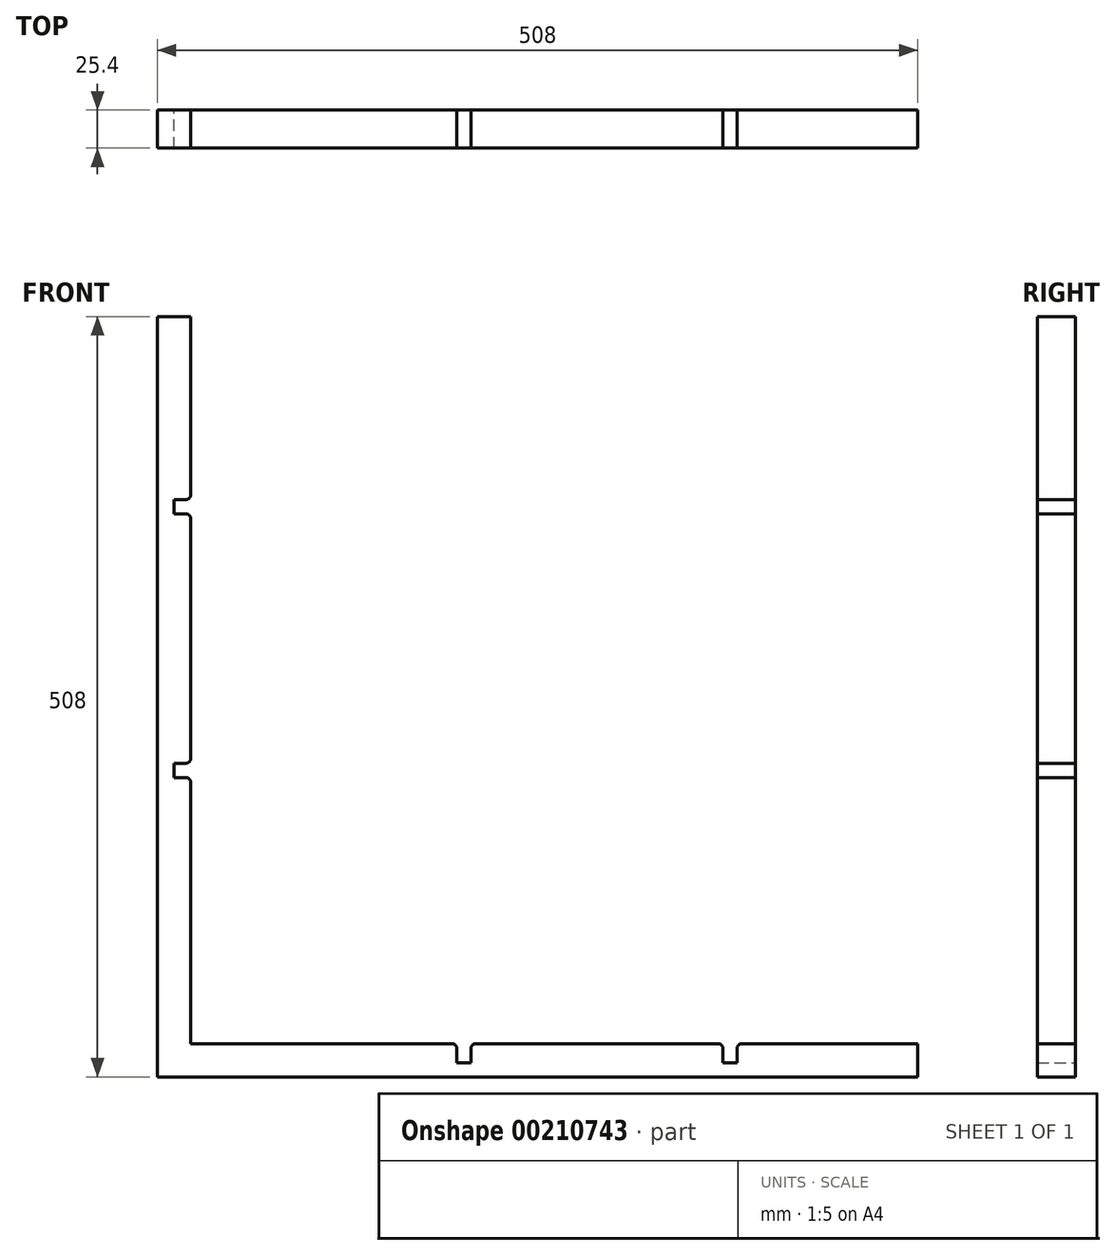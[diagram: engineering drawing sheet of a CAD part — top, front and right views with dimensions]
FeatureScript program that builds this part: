
annotation { "Feature Type Name" : "Feature", "Feature Type Description" : "" }
export const myFeature = defineFeature(function(context is Context, id is Id, definition is map)
    precondition{}
    {
        {
            var Q0;
            Q0=qCreatedBy(makeId("Front.planeOp"),FACE);
            var sketch = newSketch(context, id + "F0", { "sketchPlane" : qUnion([Q0])});
            skLineSegment(sketch, "E0", {"start": v(-317.84, 287.42) * mm, "end": v(-317.84, -220.58) * mm});
            skLineSegment(sketch, "E1", {"start": v(-317.84, -220.58) * mm, "end": v(190.16, -220.58) * mm});
            skLineSegment(sketch, "E2", {"start": v(-295.62, 287.42) * mm, "end": v(-317.84, 287.42) * mm});
            skLineSegment(sketch, "E3", {"start": v(190.16, -220.58) * mm, "end": v(190.16, -198.36) * mm});
            skLineSegment(sketch, "E4", {"start": v(190.16, -198.36) * mm, "end": v(72.68, -198.36) * mm});
            skLineSegment(sketch, "E5", {"start": v(69.5, -201.53) * mm, "end": v(69.5, -211.06) * mm});
            skLineSegment(sketch, "E6", {"start": v(69.5, -211.06) * mm, "end": v(59.98, -211.06) * mm});
            skLineSegment(sketch, "E7", {"start": v(59.98, -211.06) * mm, "end": v(59.98, -201.53) * mm});
            skLineSegment(sketch, "E8", {"start": v(56.8, -198.36) * mm, "end": v(-105.12, -198.36) * mm});
            skLineSegment(sketch, "E9", {"start": v(-108.3, -201.53) * mm, "end": v(-108.3, -211.06) * mm});
            skLineSegment(sketch, "E10", {"start": v(-108.3, -211.06) * mm, "end": v(-117.82, -211.06) * mm});
            skLineSegment(sketch, "E11", {"start": v(-117.82, -211.06) * mm, "end": v(-117.82, -201.53) * mm});
            skLineSegment(sketch, "E12", {"start": v(-121, -198.36) * mm, "end": v(-295.62, -198.36) * mm});
            skLineSegment(sketch, "E13", {"start": v(-295.62, -198.36) * mm, "end": v(-295.62, -23.73) * mm});
            skLineSegment(sketch, "E14", {"start": v(-298.8, -20.56) * mm, "end": v(-306.67, -20.56) * mm});
            skLineSegment(sketch, "E15", {"start": v(-306.67, -20.56) * mm, "end": v(-306.67, -11.03) * mm});
            skLineSegment(sketch, "E16", {"start": v(-306.67, -11.03) * mm, "end": v(-298.8, -11.03) * mm});
            skLineSegment(sketch, "E17", {"start": v(-295.62, -7.86) * mm, "end": v(-295.62, 152.42) * mm});
            skLineSegment(sketch, "E18", {"start": v(-298.8, 155.6) * mm, "end": v(-306.67, 155.6) * mm});
            skLineSegment(sketch, "E19", {"start": v(-306.67, 155.6) * mm, "end": v(-306.67, 165.12) * mm});
            skLineSegment(sketch, "E20", {"start": v(-306.67, 165.12) * mm, "end": v(-298.8, 165.12) * mm});
            skLineSegment(sketch, "E21", {"start": v(-295.62, 168.3) * mm, "end": v(-295.62, 287.42) * mm});
            skPoint(sketch, "E22.visualSharp", {"position": v(-295.62, 165.12) * mm});
            skArc(sketch, "E22.filletArc", {"start": v(-298.8, 165.12) * mm, "mid": v(-296.55, 166.05) * mm, "end": v(-295.62, 168.3) * mm});
            skPoint(sketch, "E23.visualSharp", {"position": v(-295.62, 155.6) * mm});
            skArc(sketch, "E23.filletArc", {"start": v(-295.62, 152.42) * mm, "mid": v(-296.55, 154.66) * mm, "end": v(-298.8, 155.6) * mm});
            skPoint(sketch, "E24.visualSharp", {"position": v(-295.62, -11.03) * mm});
            skArc(sketch, "E24.filletArc", {"start": v(-298.8, -11.03) * mm, "mid": v(-296.55, -10.1) * mm, "end": v(-295.62, -7.86) * mm});
            skPoint(sketch, "E25.visualSharp", {"position": v(-295.62, -20.56) * mm});
            skArc(sketch, "E25.filletArc", {"start": v(-295.62, -23.73) * mm, "mid": v(-296.55, -21.49) * mm, "end": v(-298.8, -20.56) * mm});
            skPoint(sketch, "E26.visualSharp", {"position": v(-108.3, -198.36) * mm});
            skArc(sketch, "E26.filletArc", {"start": v(-105.12, -198.36) * mm, "mid": v(-107.36, -199.29) * mm, "end": v(-108.3, -201.53) * mm});
            skPoint(sketch, "E27.visualSharp", {"position": v(-117.82, -198.36) * mm});
            skArc(sketch, "E27.filletArc", {"start": v(-117.82, -201.53) * mm, "mid": v(-118.75, -199.29) * mm, "end": v(-121, -198.36) * mm});
            skPoint(sketch, "E28.visualSharp", {"position": v(69.5, -198.36) * mm});
            skArc(sketch, "E28.filletArc", {"start": v(72.68, -198.36) * mm, "mid": v(70.44, -199.29) * mm, "end": v(69.5, -201.53) * mm});
            skPoint(sketch, "E29.visualSharp", {"position": v(59.98, -198.36) * mm});
            skArc(sketch, "E29.filletArc", {"start": v(59.98, -201.53) * mm, "mid": v(59.05, -199.29) * mm, "end": v(56.8, -198.36) * mm});
            skSolve(sketch);
        }
        {
            var Q0;
            Q0 = qSketchRegion(id + "F0", true);
            extrude(context, id + "F1", {"entities" : qUnion([Q0]), "depth" : 25.4 * mm});
        }
        {
            var Q0;
            Q0 = qSketchRegion(id + "F0", true);
            extrude(context, id + "F2", {"entities" : qUnion([Q0]), "operationType" : NewBodyOperationType.ADD, "depth" : 25.4 * mm});
        }
    });
